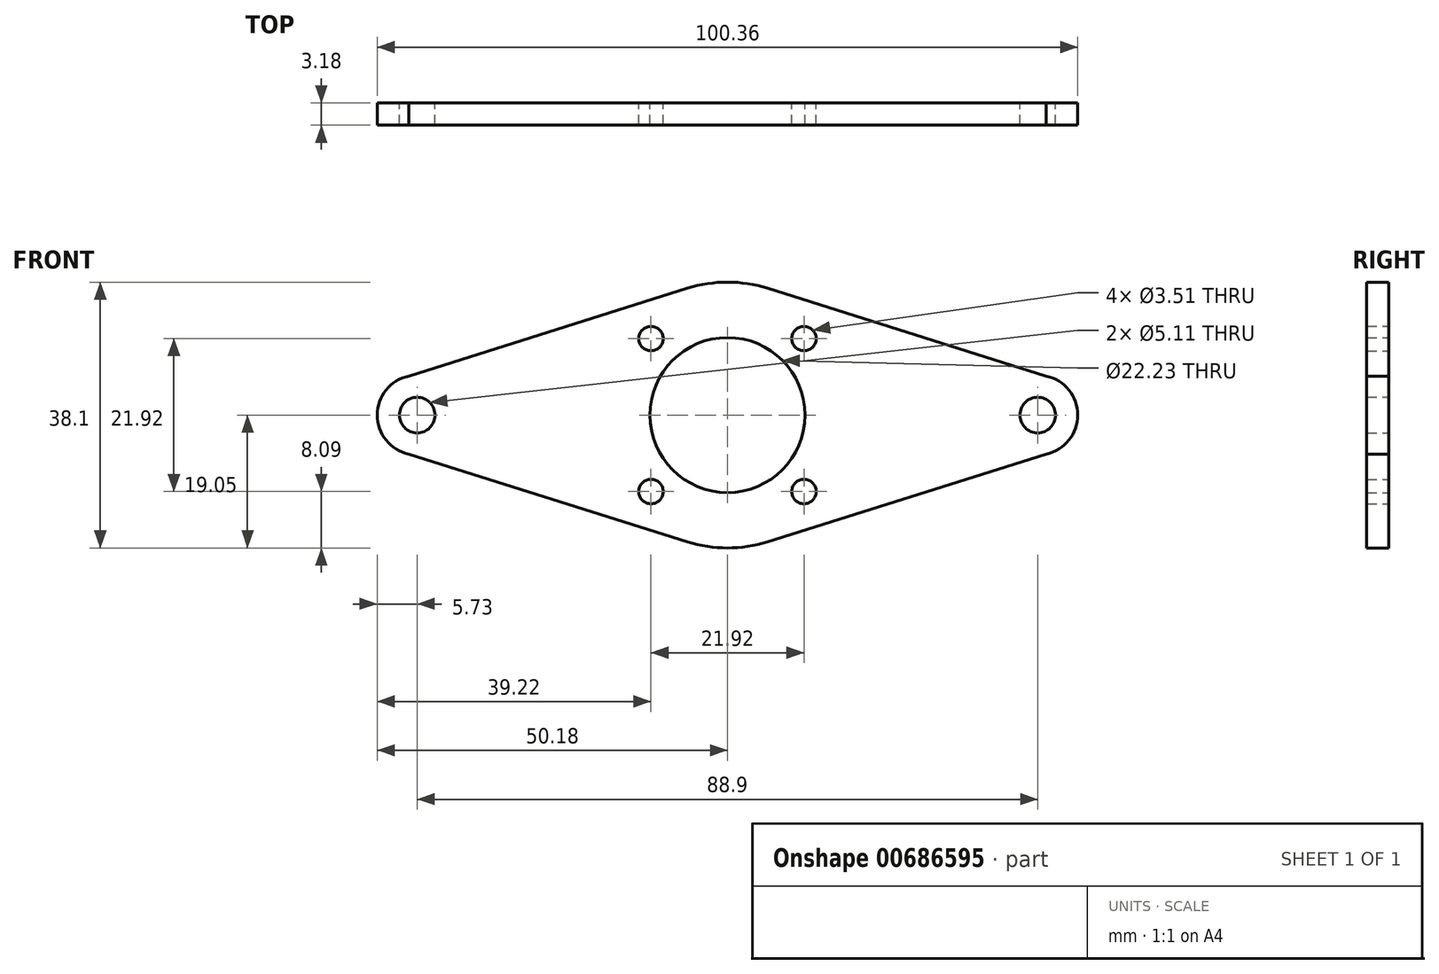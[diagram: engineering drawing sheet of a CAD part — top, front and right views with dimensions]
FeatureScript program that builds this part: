
annotation { "Feature Type Name" : "Feature", "Feature Type Description" : "" }
export const myFeature = defineFeature(function(context is Context, id is Id, definition is map)
    precondition{}
    {
        {
            var Q0;
            Q0=qCreatedBy(makeId("Front.planeOp"),FACE);
            var sketch = newSketch(context, id + "F0", { "sketchPlane" : qUnion([Q0])});
            skLineSegment(sketch, "E0.bottom", {"start": v(-10.96, 10.96) * mm, "end": v(10.96, 10.96) * mm, "construction": true});
            skLineSegment(sketch, "E0.top", {"start": v(-10.96, -10.96) * mm, "end": v(10.96, -10.96) * mm, "construction": true});
            skLineSegment(sketch, "E0.left", {"start": v(-10.96, 10.96) * mm, "end": v(-10.96, -10.96) * mm, "construction": true});
            skLineSegment(sketch, "E0.right", {"start": v(10.96, 10.96) * mm, "end": v(10.96, -10.96) * mm, "construction": true});
            skPoint(sketch, "E0.middle", {"position": v(0, 0) * mm});
            skCircle(sketch, "E1", {"center": v(-10.96, -10.96) * mm, "radius": 1.75 * mm});
            skCircle(sketch, "E2", {"center": v(10.96, -10.96) * mm, "radius": 1.75 * mm});
            skCircle(sketch, "E3", {"center": v(10.96, 10.96) * mm, "radius": 1.75 * mm});
            skCircle(sketch, "E4", {"center": v(-10.96, 10.96) * mm, "radius": 1.75 * mm});
            skLineSegment(sketch, "E5", {"start": v(-44.45, 0) * mm, "end": v(0, 0) * mm, "construction": true});
            skLineSegment(sketch, "E6", {"start": v(0, 0) * mm, "end": v(44.45, 0) * mm, "construction": true});
            skCircle(sketch, "E7", {"center": v(-44.45, 0) * mm, "radius": 2.55 * mm});
            skCircle(sketch, "E8", {"center": v(44.45, 0) * mm, "radius": 2.55 * mm});
            skArc(sketch, "E9", {"start": v(-45.68, 5.6) * mm, "mid": v(-50.18, 0) * mm, "end": v(-45.68, -5.6) * mm});
            skArc(sketch, "E10", {"start": v(45.68, -5.6) * mm, "mid": v(50.18, 0) * mm, "end": v(45.68, 5.6) * mm});
            skArc(sketch, "E11", {"start": v(-5.72, -18.17) * mm, "mid": v(0, -19.05) * mm, "end": v(5.72, -18.17) * mm});
            skLineSegment(sketch, "E12", {"start": v(-46.64, 5.3) * mm, "end": v(-5.72, 18.17) * mm});
            skLineSegment(sketch, "E13", {"start": v(0, 4.97) * mm, "end": v(0, -4.45) * mm, "construction": true});
            skLineSegment(sketch, "E14.MirrorCS", {"start": v(-46.64, -5.3) * mm, "end": v(-5.72, -18.17) * mm});
            skLineSegment(sketch, "E15.MirrorCS", {"start": v(46.64, -5.3) * mm, "end": v(5.72, -18.17) * mm});
            skLineSegment(sketch, "E16.MirrorCS", {"start": v(46.64, 5.3) * mm, "end": v(5.72, 18.17) * mm});
            skArc(sketch, "E17.trimOffspring", {"start": v(5.72, 18.17) * mm, "mid": v(0, 19.05) * mm, "end": v(-5.72, 18.17) * mm});
            skCircle(sketch, "E18", {"center": v(0, 0) * mm, "radius": 11.11 * mm});
            skSolve(sketch);
        }
        {
            var Q0;
            Q0 = qSketchRegion(id + "F0", true);
            extrude(context, id + "F1", {"entities" : qUnion([Q0]), "depth" : 3.17 * mm, "offsetDistance" : 25.4 * mm});
        }
    });
